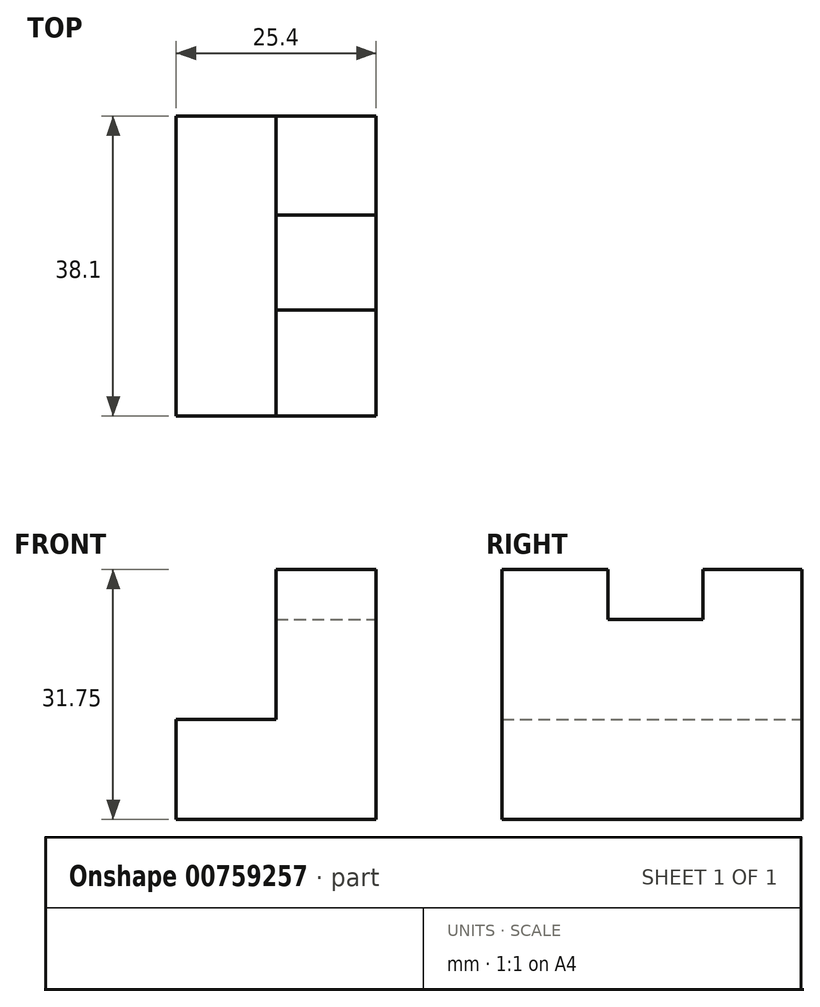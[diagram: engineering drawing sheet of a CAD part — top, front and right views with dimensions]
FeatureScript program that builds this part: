
annotation { "Feature Type Name" : "Feature", "Feature Type Description" : "" }
export const myFeature = defineFeature(function(context is Context, id is Id, definition is map)
    precondition{}
    {
        {
            var Q0;
            Q0=qCreatedBy(makeId("Front.planeOp"),FACE);
            var sketch = newSketch(context, id + "F0", { "sketchPlane" : qUnion([Q0])});
            skLineSegment(sketch, "E0", {"start": v(0, 0) * mm, "end": v(25.4, 0) * mm});
            skLineSegment(sketch, "E1", {"start": v(25.4, 0) * mm, "end": v(25.4, 31.75) * mm});
            skLineSegment(sketch, "E2", {"start": v(25.4, 31.75) * mm, "end": v(12.7, 31.75) * mm});
            skLineSegment(sketch, "E3", {"start": v(12.7, 31.75) * mm, "end": v(12.7, 12.7) * mm});
            skLineSegment(sketch, "E4", {"start": v(12.7, 12.7) * mm, "end": v(0, 12.7) * mm});
            skLineSegment(sketch, "E5", {"start": v(0, 12.7) * mm, "end": v(0, 0) * mm});
            skSolve(sketch);
        }
        {
            var Q0;
            Q0=makeQuery(id+"F0.imprint","IMPRINT",FACE,{"disambiguationData":[TD([[makeQuery(id+"F0.imprint","IMPRINT",EDGE,{"derivedFrom":sQuery(id+"F0.wireOp",EDGE,"E0")}),1.0]])]});
            extrude(context, id + "F1", {"entities" : qUnion([Q0]), "depth" : 38.1 * mm, "offsetDistance" : 25.4 * mm});
        }
        {
            var Q0;
            Q0=makeQuery(id+"F1.opExtrude","SWEPT_FACE",FACE,{"disambiguationData":[OSD([sQuery(id+"F0.wireOp",EDGE,"E2")])]});
            var sketch = newSketch(context, id + "F2", { "sketchPlane" : qUnion([Q0])});
            skLineSegment(sketch, "E6", {"start": v(12.7, -12.56) * mm, "end": v(25.4, -12.56) * mm});
            skLineSegment(sketch, "E7", {"start": v(12.7, -24.65) * mm, "end": v(25.4, -24.65) * mm});
            skSolve(sketch);
        }
        {
            var Q0;
            {var subQ0=sQuery(id+"F2.wireOp",EDGE,"E6");Q0=makeQuery(id+"F2.imprint","IMPRINT",FACE,{"disambiguationData":[TD([[makeQuery(id+"F2.imprint","IMPRINT",EDGE,{"derivedFrom":subQ0}),-1.0]])]});}
            extrude(context, id + "F3", {"entities" : qUnion([Q0]), "operationType" : NewBodyOperationType.REMOVE, "oppositeDirection" : true, "depth" : 6.35 * mm, "offsetDistance" : 25.4 * mm});
        }
    });
